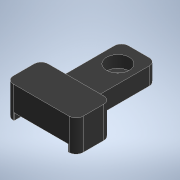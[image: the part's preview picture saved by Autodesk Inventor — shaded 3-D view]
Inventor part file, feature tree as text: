
AUTODESK INVENTOR PART (.ipt)
format: ipt  version: 2022.2 (Build 262287010, 287A)  size: 155,648 bytes
history: native  units: mm
features: sketch x4, extrude x3, fillet x2, hole x1, mirror x1
ambient origin geometry x8: Origin, YZ Plane, XZ Plane, XY Plane, X Axis, Y Axis, Z Axis, Center Point
bodies: Volumenkörper1 (feature_tree)
feature tree (11):
  extrude  "Extrusion1"  Depth=10.0mm
  hole  "Bohrung1"  [1 undecoded]
  extrude  "Extrusion2"  Depth=2.0mm
  extrude  "Extrusion3"  Depth=2.0mm TaperAngle=0.0deg
  mirror  "Spiegeln1"
  fillet  "Rundung1"  Radius=2.25mm
  fillet  "Rundung2"  Radius=2.0mm
  sketch  "Skizze1"  dims[d0=20.0mm d1=10.0mm]
  sketch  "Skizze2"  dims[d2=10.0mm d3=18.0mm]
  sketch  "Skizze3"  dims[d4=5.0mm d5=0.0mm]
  sketch  "Skizze4"  dims[d7=3.4mm d8=6.0mm d9=6.5mm d10=3.4mm d11=14.3117mm d12=8.0mm d13=20.594885mm d14=22.0mm d15=2.0mm d16=0.0mm d17=2.25mm d18=2.0mm d19=0.0mm d23=2.0mm d24=2.0mm]
note: 1 required parameter value undecoded (feature->parameter linkage not recoverable at this tier; creation-order binding heuristic only, values carry confidence <= 0.55)
